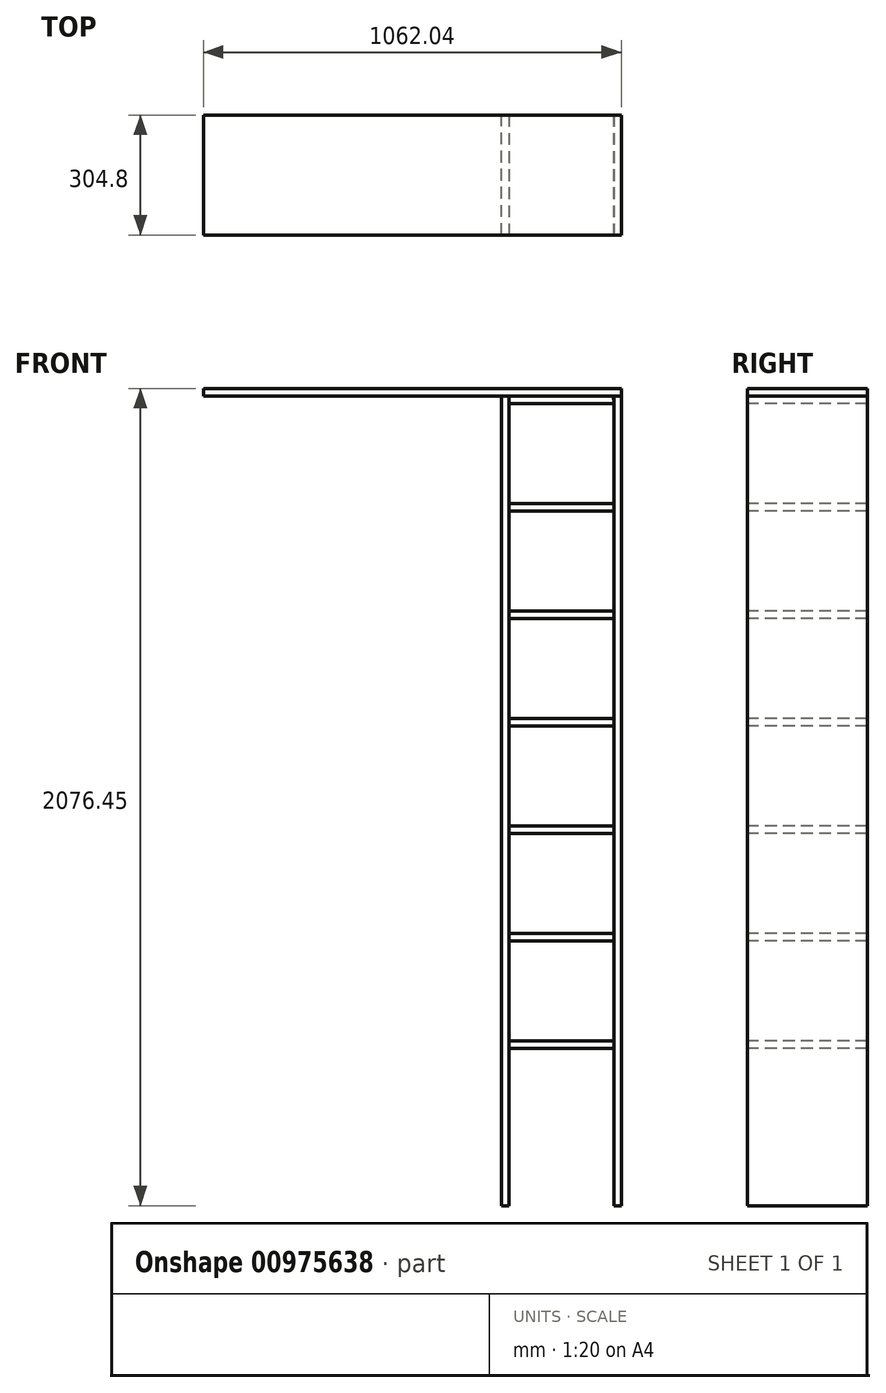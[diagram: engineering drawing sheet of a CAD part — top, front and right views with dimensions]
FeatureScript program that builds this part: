
annotation { "Feature Type Name" : "Feature", "Feature Type Description" : "" }
export const myFeature = defineFeature(function(context is Context, id is Id, definition is map)
    precondition{}
    {
        {
            var Q0;
            Q0=qCreatedBy(makeId("Front.planeOp"),FACE);
            var sketch = newSketch(context, id + "F0", { "sketchPlane" : qUnion([Q0])});
            skLineSegment(sketch, "E0.bottom", {"start": v(-432.92, 1017.43) * mm, "end": v(-413.87, 1017.43) * mm});
            skLineSegment(sketch, "E0.top", {"start": v(-432.92, -1039.97) * mm, "end": v(-413.87, -1039.97) * mm});
            skLineSegment(sketch, "E0.left", {"start": v(-432.92, 1017.43) * mm, "end": v(-432.92, -1039.97) * mm});
            skLineSegment(sketch, "E0.right", {"start": v(-413.87, 1017.43) * mm, "end": v(-413.87, -1039.97) * mm});
            skLineSegment(sketch, "E1.bottom", {"start": v(-147.17, 1017.43) * mm, "end": v(-128.12, 1017.43) * mm});
            skLineSegment(sketch, "E1.top", {"start": v(-147.17, -1039.97) * mm, "end": v(-128.12, -1039.97) * mm});
            skLineSegment(sketch, "E1.left", {"start": v(-128.12, 1017.43) * mm, "end": v(-128.12, -1039.97) * mm});
            skLineSegment(sketch, "E1.right", {"start": v(-147.17, 1017.43) * mm, "end": v(-147.17, -1039.97) * mm});
            skSolve(sketch);
        }
        {
            var Q0;
            Q0 = qSketchRegion(id + "F0", true);
            extrude(context, id + "F1", {"entities" : qUnion([Q0]), "depth" : 304.8 * mm, "offsetDistance" : 25.4 * mm});
        }
        {
            var Q0;
            Q0=makeQuery(id+"F1.opExtrude","CAP_FACE",FACE,{"disambiguationData":[OSD([sQuery(id+"F0.wireOp",EDGE,"E0.bottom"),sQuery(id+"F0.wireOp",EDGE,"E0.top"),sQuery(id+"F0.wireOp",EDGE,"E0.left"),sQuery(id+"F0.wireOp",EDGE,"E0.right")])],"isStart":false});
            var sketch = newSketch(context, id + "F2", { "sketchPlane" : qUnion([Q0])});
            skLineSegment(sketch, "E2.bottom", {"start": v(-413.87, -620.87) * mm, "end": v(-147.17, -620.87) * mm});
            skLineSegment(sketch, "E2.top", {"start": v(-413.87, -639.92) * mm, "end": v(-147.17, -639.92) * mm});
            skLineSegment(sketch, "E2.left", {"start": v(-413.87, -620.87) * mm, "end": v(-413.87, -639.92) * mm});
            skLineSegment(sketch, "E2.right", {"start": v(-147.17, -620.87) * mm, "end": v(-147.17, -639.92) * mm});
            skLineSegment(sketch, "E3.bottom", {"start": v(-413.87, -347.82) * mm, "end": v(-147.17, -347.82) * mm});
            skLineSegment(sketch, "E3.top", {"start": v(-413.87, -366.87) * mm, "end": v(-147.17, -366.87) * mm});
            skLineSegment(sketch, "E3.left", {"start": v(-413.87, -347.82) * mm, "end": v(-413.87, -366.87) * mm});
            skLineSegment(sketch, "E3.right", {"start": v(-147.17, -347.82) * mm, "end": v(-147.17, -366.87) * mm});
            skLineSegment(sketch, "E4.bottom", {"start": v(-413.87, -74.77) * mm, "end": v(-147.17, -74.77) * mm});
            skLineSegment(sketch, "E4.top", {"start": v(-413.87, -93.82) * mm, "end": v(-147.17, -93.82) * mm});
            skLineSegment(sketch, "E4.left", {"start": v(-413.87, -74.77) * mm, "end": v(-413.87, -93.82) * mm});
            skLineSegment(sketch, "E4.right", {"start": v(-147.17, -74.77) * mm, "end": v(-147.17, -93.82) * mm});
            skLineSegment(sketch, "E5.bottom", {"start": v(-413.87, 198.28) * mm, "end": v(-147.17, 198.28) * mm});
            skLineSegment(sketch, "E5.top", {"start": v(-413.87, 179.23) * mm, "end": v(-147.17, 179.23) * mm});
            skLineSegment(sketch, "E5.left", {"start": v(-413.87, 198.28) * mm, "end": v(-413.87, 179.23) * mm});
            skLineSegment(sketch, "E5.right", {"start": v(-147.17, 198.28) * mm, "end": v(-147.17, 179.23) * mm});
            skLineSegment(sketch, "E6.bottom", {"start": v(-413.87, 471.33) * mm, "end": v(-147.17, 471.33) * mm});
            skLineSegment(sketch, "E6.top", {"start": v(-413.87, 452.28) * mm, "end": v(-147.17, 452.28) * mm});
            skLineSegment(sketch, "E6.left", {"start": v(-413.87, 471.33) * mm, "end": v(-413.87, 452.28) * mm});
            skLineSegment(sketch, "E6.right", {"start": v(-147.17, 471.33) * mm, "end": v(-147.17, 452.28) * mm});
            skLineSegment(sketch, "E7.bottom", {"start": v(-413.87, 744.38) * mm, "end": v(-147.17, 744.38) * mm});
            skLineSegment(sketch, "E7.top", {"start": v(-413.87, 725.33) * mm, "end": v(-147.17, 725.33) * mm});
            skLineSegment(sketch, "E7.left", {"start": v(-413.87, 744.38) * mm, "end": v(-413.87, 725.33) * mm});
            skLineSegment(sketch, "E7.right", {"start": v(-147.17, 744.38) * mm, "end": v(-147.17, 725.33) * mm});
            skLineSegment(sketch, "E8.bottom", {"start": v(-413.87, 1017.43) * mm, "end": v(-148.72, 1017.43) * mm});
            skLineSegment(sketch, "E8.top", {"start": v(-413.87, 998.38) * mm, "end": v(-147.17, 998.38) * mm});
            skLineSegment(sketch, "E8.left", {"start": v(-413.87, 1017.43) * mm, "end": v(-413.87, 998.38) * mm});
            skLineSegment(sketch, "E8.right", {"start": v(-148.72, 1017.43) * mm, "end": v(-147.17, 998.38) * mm});
            skSolve(sketch);
        }
        {
            var Q0;
            Q0 = qSketchRegion(id + "F2", true);
            extrude(context, id + "F3", {"entities" : qUnion([Q0]), "oppositeDirection" : true, "depth" : 304.8 * mm, "offsetDistance" : 25.4 * mm});
        }
        {
            var Q0;
            Q0=qCreatedBy(makeId("Front.planeOp"),FACE);
            var sketch = newSketch(context, id + "F4", { "sketchPlane" : qUnion([Q0])});
            skLineSegment(sketch, "E9.bottom", {"start": v(-128.12, 1017.43) * mm, "end": v(-1190.16, 1017.43) * mm});
            skLineSegment(sketch, "E9.top", {"start": v(-128.12, 1036.48) * mm, "end": v(-1190.16, 1036.48) * mm});
            skLineSegment(sketch, "E9.left", {"start": v(-128.12, 1017.43) * mm, "end": v(-128.12, 1036.48) * mm});
            skLineSegment(sketch, "E9.right", {"start": v(-1190.16, 1017.43) * mm, "end": v(-1190.16, 1036.48) * mm});
            skSolve(sketch);
        }
        {
            var Q0;
            Q0 = qSketchRegion(id + "F4", true);
            extrude(context, id + "F5", {"entities" : qUnion([Q0]), "depth" : 304.8 * mm, "offsetDistance" : 25.4 * mm});
        }
    });
